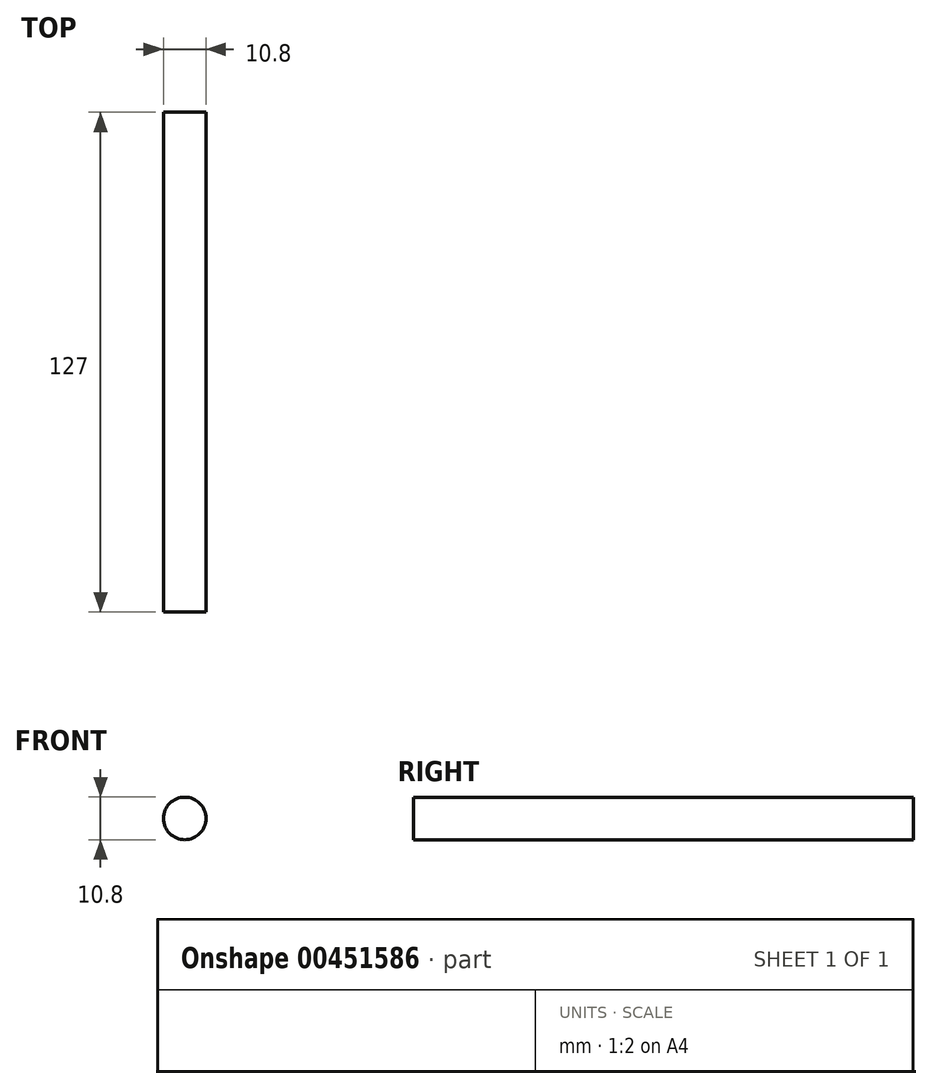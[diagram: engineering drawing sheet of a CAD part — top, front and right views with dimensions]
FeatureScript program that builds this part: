
annotation { "Feature Type Name" : "Feature", "Feature Type Description" : "" }
export const myFeature = defineFeature(function(context is Context, id is Id, definition is map)
    precondition{}
    {
        {
            var Q0;
            Q0=qCreatedBy(makeId("Front.planeOp"),FACE);
            var sketch = newSketch(context, id + "F0", { "sketchPlane" : qUnion([Q0])});
            skCircle(sketch, "E0", {"center": v(0, 0) * mm, "radius": 5.4 * mm});
            skSolve(sketch);
        }
        {
            var Q0;
            Q0=makeQuery(id+"F0.imprint","IMPRINT",FACE,{"disambiguationData":[TD([[makeQuery(id+"F0.imprint","IMPRINT",EDGE,{"derivedFrom":sQuery(id+"F0.wireOp",EDGE,"E0")}),1.0]])]});
            extrude(context, id + "F1", {"entities" : qUnion([Q0]), "endBound" : BoundingType.SYMMETRIC, "depth" : 127 * mm});
        }
    });
